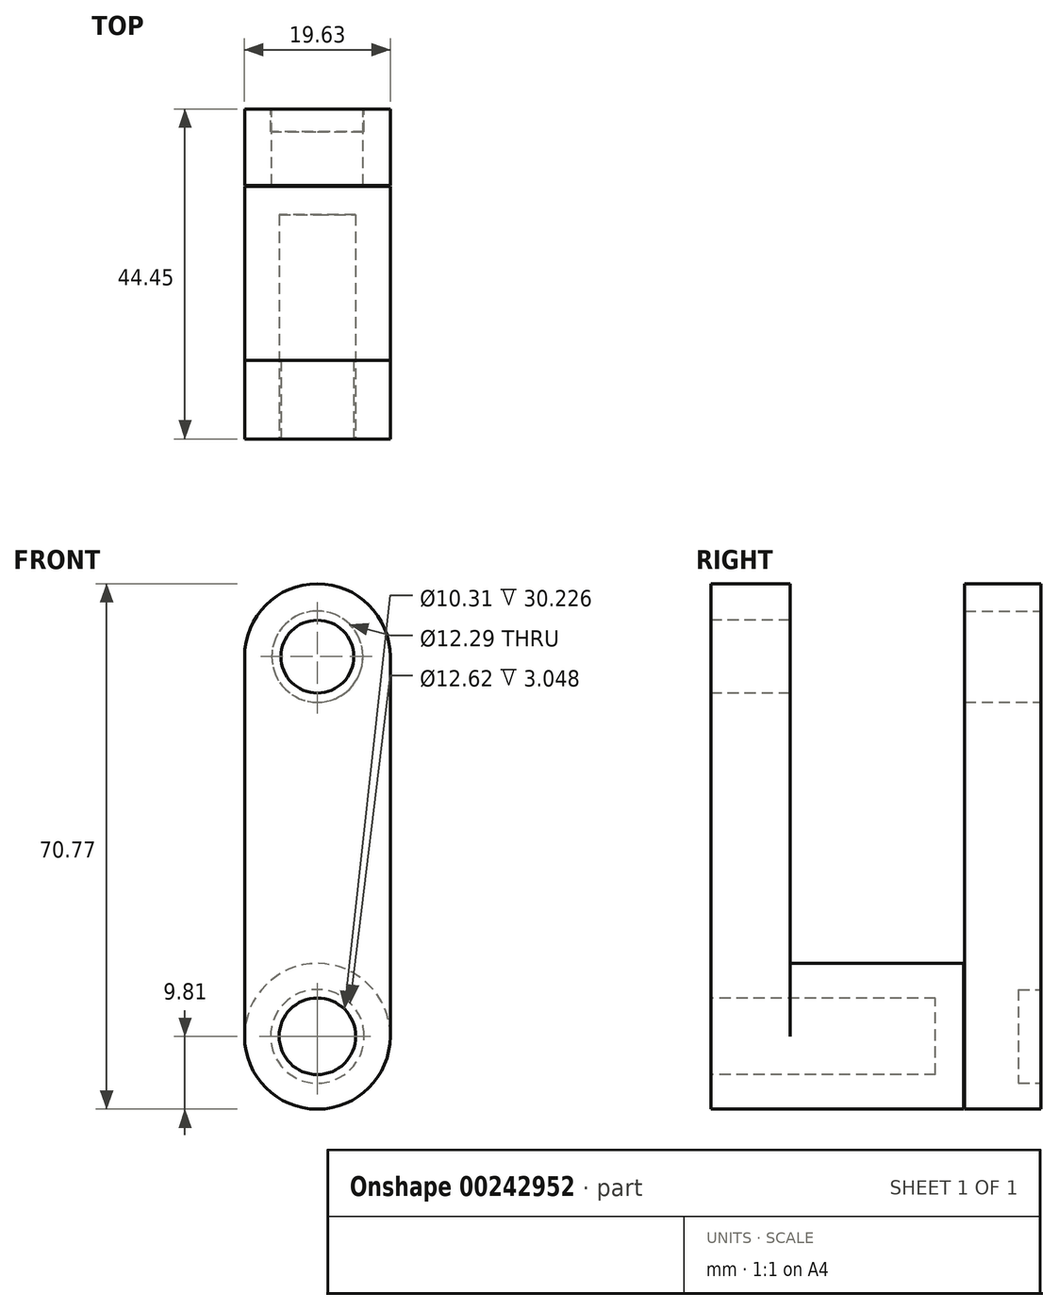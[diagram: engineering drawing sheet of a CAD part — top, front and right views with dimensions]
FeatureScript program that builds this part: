
annotation { "Feature Type Name" : "Feature", "Feature Type Description" : "" }
export const myFeature = defineFeature(function(context is Context, id is Id, definition is map)
    precondition{}
    {
        {
            var Q0;
            Q0=qCreatedBy(makeId("Front.planeOp"),FACE);
            var sketch = newSketch(context, id + "F0", { "sketchPlane" : qUnion([Q0])});
            skLineSegment(sketch, "E0", {"start": v(0, 0) * mm, "end": v(0, 51.15) * mm});
            skLineSegment(sketch, "E1", {"start": v(-19.63, 51.15) * mm, "end": v(-19.63, 0) * mm});
            skArc(sketch, "E2", {"start": v(-19.63, 51.15) * mm, "mid": v(-9.81, 60.96) * mm, "end": v(0, 51.15) * mm});
            skArc(sketch, "E3", {"start": v(-19.63, 0) * mm, "mid": v(-9.81, -9.81) * mm, "end": v(0, 0) * mm});
            skSolve(sketch);
        }
        {
            var Q0;
            Q0=makeQuery(id+"F0.imprint","IMPRINT",FACE,{"disambiguationData":[TD([[makeQuery(id+"F0.imprint","IMPRINT",EDGE,{"derivedFrom":sQuery(id+"F0.wireOp",EDGE,"E0")}),1.0]])]});
            extrude(context, id + "F1", {"entities" : qUnion([Q0]), "oppositeDirection" : true, "depth" : 44.45 * mm});
        }
        {
            var Q0;
            Q0=qCreatedBy(makeId("Right.planeOp"),FACE);
            var sketch = newSketch(context, id + "F2", { "sketchPlane" : qUnion([Q0])});
            skLineSegment(sketch, "E4.bottom", {"start": v(10.62, 64.08) * mm, "end": v(34.17, 64.08) * mm});
            skLineSegment(sketch, "E4.top", {"start": v(10.62, -13.05) * mm, "end": v(34.17, -13.05) * mm});
            skLineSegment(sketch, "E4.left", {"start": v(10.62, 64.08) * mm, "end": v(10.62, -13.05) * mm});
            skLineSegment(sketch, "E4.right", {"start": v(34.17, 64.08) * mm, "end": v(34.17, -13.05) * mm});
            skSolve(sketch);
        }
        {
            var Q0;
            Q0=qSketchRegion(id+"F2",true);
            extrude(context, id + "F3", {"entities" : qUnion([Q0]), "operationType" : NewBodyOperationType.REMOVE, "oppositeDirection" : true, "depth" : 101.6 * mm});
        }
        {
            var Q0;
            Q0=makeQuery(id+"F1.opExtrude","CAP_FACE",FACE,{"disambiguationData":[OSD([sQuery(id+"F0.wireOp",EDGE,"E0"),sQuery(id+"F0.wireOp",EDGE,"E1"),sQuery(id+"F0.wireOp",EDGE,"E2"),sQuery(id+"F0.wireOp",EDGE,"E3")])],"isStart":true});
            var sketch = newSketch(context, id + "F4", { "sketchPlane" : qUnion([Q0])});
            skCircle(sketch, "E5", {"center": v(-9.81, 0) * mm, "radius": 4.02 * mm});
            skCircle(sketch, "E6", {"center": v(-9.81, 51.15) * mm, "radius": 4.9 * mm});
            skSolve(sketch);
        }
        {
            var Q0;
            Q0=makeQuery(id+"F4.imprint","IMPRINT",FACE,{"disambiguationData":[TD([[makeQuery(id+"F4.imprint","IMPRINT",EDGE,{"derivedFrom":sQuery(id+"F4.wireOp",EDGE,"E6")}),1.0]])]});
            extrude(context, id + "F5", {"entities" : qUnion([Q0]), "operationType" : NewBodyOperationType.REMOVE, "oppositeDirection" : true, "depth" : 74.93 * mm});
        }
        {
            var Q0;
            Q0=makeQuery(id+"F1.opExtrude","CAP_FACE",FACE,{"disambiguationData":[OSD([sQuery(id+"F0.wireOp",EDGE,"E0"),sQuery(id+"F0.wireOp",EDGE,"E1"),sQuery(id+"F0.wireOp",EDGE,"E2"),sQuery(id+"F0.wireOp",EDGE,"E3")])],"isStart":true});
            var sketch = newSketch(context, id + "F6", { "sketchPlane" : qUnion([Q0])});
            skArc(sketch, "E7", {"start": v(0, 0) * mm, "mid": v(-9.81, 9.81) * mm, "end": v(-19.63, 0) * mm});
            skSolve(sketch);
        }
        {
            var Q0;
            Q0=makeQuery(id+"F6.imprint","IMPRINT",FACE,{"disambiguationData":[TD([[makeQuery(id+"F6.imprint","IMPRINT",EDGE,{"derivedFrom":sQuery(id+"F6.wireOp",EDGE,"E7")}),1.0]])]});
            extrude(context, id + "F7", {"entities" : qUnion([Q0]), "operationType" : NewBodyOperationType.ADD, "oppositeDirection" : true, "depth" : 34.04 * mm});
        }
        {
            var Q0;
            Q0=makeQuery(id+"F1.opExtrude","CAP_FACE",FACE,{"disambiguationData":[OSD([sQuery(id+"F0.wireOp",EDGE,"E0"),sQuery(id+"F0.wireOp",EDGE,"E1"),sQuery(id+"F0.wireOp",EDGE,"E2"),sQuery(id+"F0.wireOp",EDGE,"E3")])],"isStart":true});
            var sketch = newSketch(context, id + "F8", { "sketchPlane" : qUnion([Q0])});
            skCircle(sketch, "E8", {"center": v(-9.81, 0) * mm, "radius": 5.16 * mm});
            skSolve(sketch);
        }
        {
            var Q0;
            Q0=makeQuery(id+"F8.imprint","IMPRINT",FACE,{"disambiguationData":[TD([[makeQuery(id+"F8.imprint","IMPRINT",EDGE,{"derivedFrom":sQuery(id+"F8.wireOp",EDGE,"E8")}),1.0]])]});
            extrude(context, id + "F9", {"entities" : qUnion([Q0]), "operationType" : NewBodyOperationType.REMOVE, "oppositeDirection" : true, "depth" : 30.23 * mm});
        }
        {
            var Q0;
            Q0=makeQuery(id+"F1.opExtrude","CAP_FACE",FACE,{"disambiguationData":[OSD([sQuery(id+"F0.wireOp",EDGE,"E0"),sQuery(id+"F0.wireOp",EDGE,"E1"),sQuery(id+"F0.wireOp",EDGE,"E2"),sQuery(id+"F0.wireOp",EDGE,"E3")])],"isStart":false});
            var sketch = newSketch(context, id + "F10", { "sketchPlane" : qUnion([Q0])});
            skCircle(sketch, "E9", {"center": v(9.81, 51.15) * mm, "radius": 6.15 * mm});
            skCircle(sketch, "E10", {"center": v(9.81, 0) * mm, "radius": 6.14 * mm});
            skSolve(sketch);
        }
        {
            var Q0;
            Q0=makeQuery(id+"F10.imprint","IMPRINT",FACE,{"disambiguationData":[TD([[makeQuery(id+"F10.imprint","IMPRINT",EDGE,{"derivedFrom":sQuery(id+"F10.wireOp",EDGE,"E9")}),1.0]])]});
            extrude(context, id + "F11", {"entities" : qUnion([Q0]), "operationType" : NewBodyOperationType.REMOVE, "oppositeDirection" : true, "depth" : 23.62 * mm});
        }
        {
            var Q0;
            Q0=makeQuery(id+"F1.opExtrude","CAP_FACE",FACE,{"disambiguationData":[OSD([sQuery(id+"F0.wireOp",EDGE,"E0"),sQuery(id+"F0.wireOp",EDGE,"E1"),sQuery(id+"F0.wireOp",EDGE,"E2"),sQuery(id+"F0.wireOp",EDGE,"E3")])],"isStart":false});
            var sketch = newSketch(context, id + "F12", { "sketchPlane" : qUnion([Q0])});
            skCircle(sketch, "E11", {"center": v(9.81, 0) * mm, "radius": 6.3 * mm});
            skSolve(sketch);
        }
        {
            var Q0;
            Q0=makeQuery(id+"F12.imprint","IMPRINT",FACE,{"disambiguationData":[TD([[makeQuery(id+"F12.imprint","IMPRINT",EDGE,{"derivedFrom":sQuery(id+"F12.wireOp",EDGE,"E11")}),1.0]])]});
            extrude(context, id + "F13", {"entities" : qUnion([Q0]), "operationType" : NewBodyOperationType.REMOVE, "oppositeDirection" : true, "depth" : 3.05 * mm});
        }
    });
